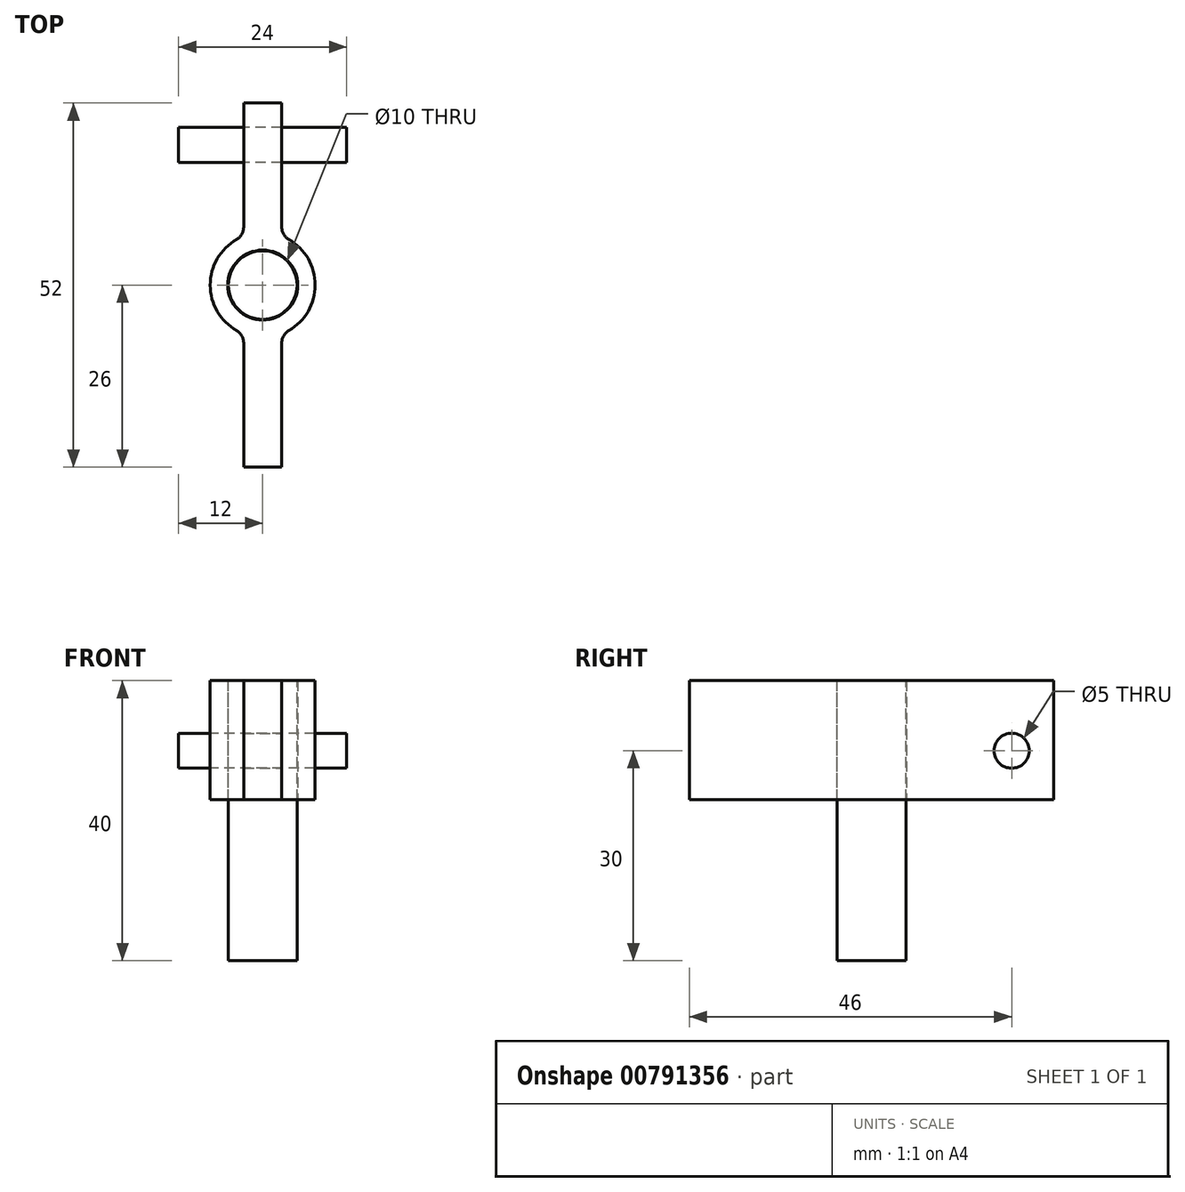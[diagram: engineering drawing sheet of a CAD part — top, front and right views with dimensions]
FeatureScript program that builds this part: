
annotation { "Feature Type Name" : "Feature", "Feature Type Description" : "" }
export const myFeature = defineFeature(function(context is Context, id is Id, definition is map)
    precondition{}
    {
        {
            var Q0;
            Q0=qCreatedBy(makeId("Top.planeOp"),FACE);
            var sketch = newSketch(context, id + "F0", { "sketchPlane" : qUnion([Q0])});
            skArc(sketch, "E0", {"start": v(-2.73, 6.99) * mm, "mid": v(-7.5, 0) * mm, "end": v(-2.72, -6.99) * mm});
            skLineSegment(sketch, "E1.bottom", {"start": v(2.72, -26) * mm, "end": v(-2.73, -26) * mm});
            skLineSegment(sketch, "E1.top", {"start": v(2.73, 26) * mm, "end": v(-2.72, 26) * mm});
            skLineSegment(sketch, "E1.left", {"start": v(2.72, -26) * mm, "end": v(2.72, -6.99) * mm});
            skLineSegment(sketch, "E1.right", {"start": v(-2.73, -26) * mm, "end": v(-2.73, -6.99) * mm});
            skLineSegment(sketch, "E2.trimOffspring", {"start": v(-2.72, 6.99) * mm, "end": v(-2.72, 26) * mm});
            skLineSegment(sketch, "E3.trimOffspring", {"start": v(2.73, 6.99) * mm, "end": v(2.73, 26) * mm});
            skArc(sketch, "E4.trimOffspring", {"start": v(2.73, -6.99) * mm, "mid": v(7.5, 0) * mm, "end": v(2.73, 6.99) * mm});
            skCircle(sketch, "E5", {"center": v(0, 0) * mm, "radius": 5 * mm});
            skSolve(sketch);
        }
        {
            var Q0;
            Q0 = qSketchRegion(id + "F0", true);
            extrude(context, id + "F1", {"entities" : qUnion([Q0]), "depth" : 17 * mm, "offsetDistance" : 25 * mm});
        }
        {
            var Q0;
            Q0=makeQuery(id+"F1.opExtrude","SWEPT_EDGE",EDGE,{"disambiguationData":[OSD([sQuery(id+"F0.wireOp",EDGE,"E0"),sQuery(id+"F0.wireOp",EDGE,"E2.trimOffspring")])]});
            var Q1;
            Q1=makeQuery(id+"F1.opExtrude","SWEPT_EDGE",EDGE,{"disambiguationData":[OSD([sQuery(id+"F0.wireOp",EDGE,"E0"),sQuery(id+"F0.wireOp",EDGE,"E1.right")])]});
            var Q2;
            Q2=makeQuery(id+"F1.opExtrude","SWEPT_EDGE",EDGE,{"disambiguationData":[OSD([sQuery(id+"F0.wireOp",EDGE,"E1.left"),sQuery(id+"F0.wireOp",EDGE,"E4.trimOffspring")])]});
            var Q3;
            Q3=makeQuery(id+"F1.opExtrude","SWEPT_EDGE",EDGE,{"disambiguationData":[OSD([sQuery(id+"F0.wireOp",EDGE,"E3.trimOffspring"),sQuery(id+"F0.wireOp",EDGE,"E4.trimOffspring")])]});
            fillet(context, id + "F2", {"entities" : qUnion([Q0, Q1, Q2, Q3]), "radius" : 2 * mm, "tangentPropagation" : true, "allowEdgeOverflow" : false});
        }
        {
            var Q0;
            Q0=makeQuery(id+"F1.opExtrude","CAP_FACE",FACE,{"disambiguationData":[OSD([sQuery(id+"F0.wireOp",EDGE,"E0"),sQuery(id+"F0.wireOp",EDGE,"E1.bottom"),sQuery(id+"F0.wireOp",EDGE,"E1.top"),sQuery(id+"F0.wireOp",EDGE,"E1.left"),sQuery(id+"F0.wireOp",EDGE,"E1.right"),sQuery(id+"F0.wireOp",EDGE,"E2.trimOffspring"),sQuery(id+"F0.wireOp",EDGE,"E3.trimOffspring"),sQuery(id+"F0.wireOp",EDGE,"E4.trimOffspring"),sQuery(id+"F0.wireOp",EDGE,"E5")])],"isStart":false});
            var sketch = newSketch(context, id + "F3", { "sketchPlane" : qUnion([Q0])});
            skCircle(sketch, "E6.0", {"center": v(0, 0) * mm, "radius": 5 * mm, "construction": true});
            skCircle(sketch, "E7.0", {"center": v(0, 0) * mm, "radius": 4.9 * mm});
            skSolve(sketch);
        }
        {
            var Q0;
            Q0 = qSketchRegion(id + "F3", true);
            extrude(context, id + "F4", {"entities" : qUnion([Q0]), "oppositeDirection" : true, "depth" : 40 * mm, "offsetDistance" : 25 * mm});
        }
        {
            var Q0;
            Q0=qCreatedBy(makeId("Right.planeOp"),FACE);
            var sketch = newSketch(context, id + "F5", { "sketchPlane" : qUnion([Q0])});
            skCircle(sketch, "E8", {"center": v(20, 7) * mm, "radius": 2.5 * mm});
            skSolve(sketch);
        }
        {
            var Q0;
            Q0 = qSketchRegion(id + "F5", true);
            extrude(context, id + "F6", {"entities" : qUnion([Q0]), "operationType" : NewBodyOperationType.REMOVE, "oppositeDirection" : true, "depth" : 10 * mm, "offsetDistance" : 25 * mm, "symmetric" : true});
        }
        {
            var Q0;
            Q0=qCreatedBy(makeId("Right.planeOp"),FACE);
            var sketch = newSketch(context, id + "F7", { "sketchPlane" : qUnion([Q0])});
            skCircle(sketch, "E9.0", {"center": v(20, 7) * mm, "radius": 2.5 * mm});
            skSolve(sketch);
        }
        {
            var Q0;
            Q0 = qSketchRegion(id + "F7", true);
            extrude(context, id + "F8", {"entities" : qUnion([Q0]), "depth" : 24 * mm, "offsetDistance" : 25 * mm, "symmetric" : true});
        }
    });
